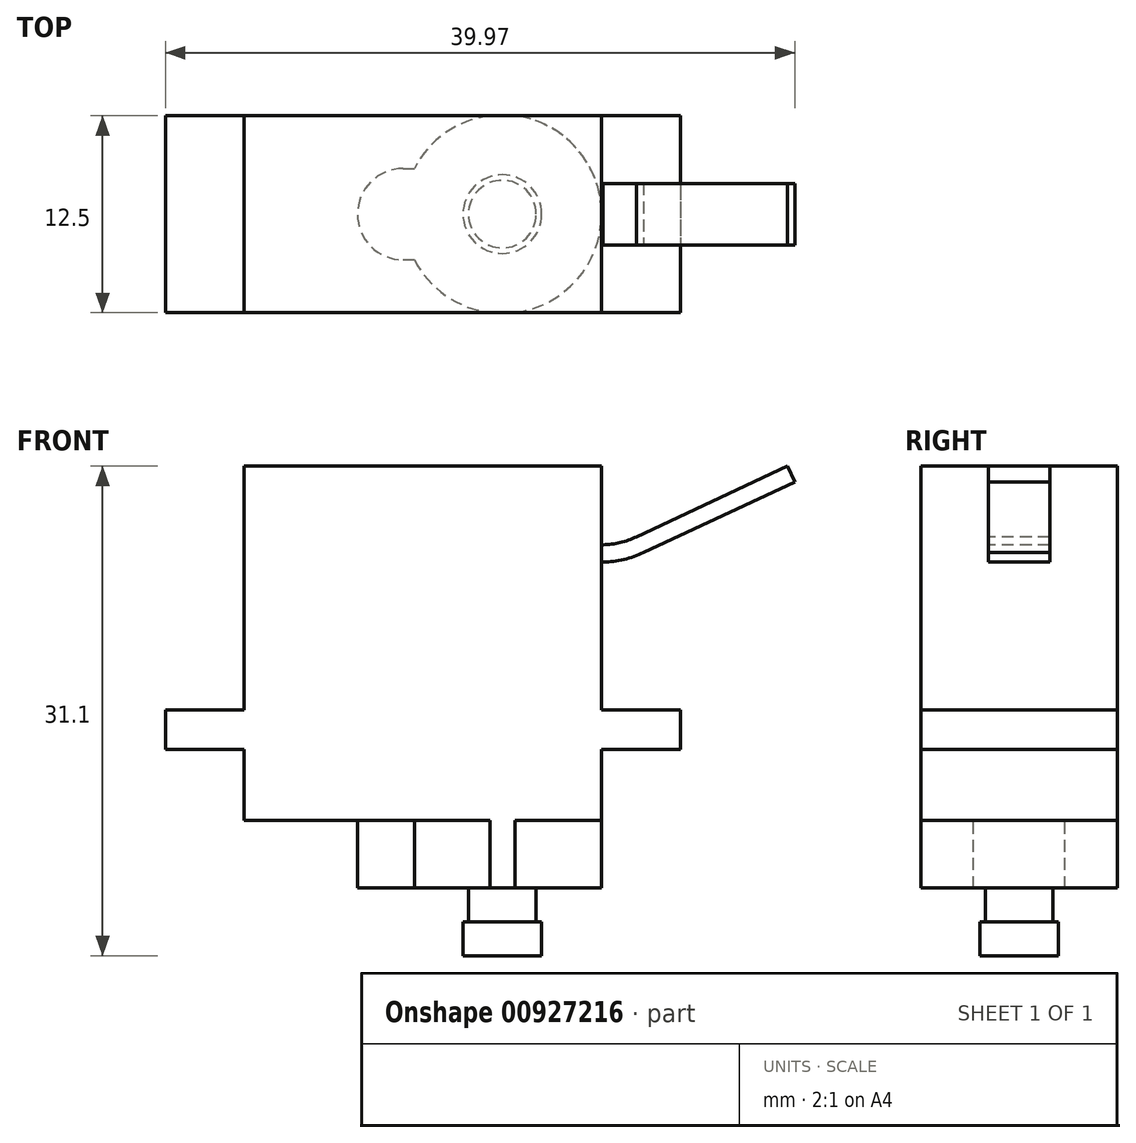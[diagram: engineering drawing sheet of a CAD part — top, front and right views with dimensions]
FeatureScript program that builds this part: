
annotation { "Feature Type Name" : "Feature", "Feature Type Description" : "" }
export const myFeature = defineFeature(function(context is Context, id is Id, definition is map)
    precondition{}
    {
        {
            var Q0;
            Q0=qCreatedBy(makeId("Top.planeOp"),FACE);
            var sketch = newSketch(context, id + "F0", { "sketchPlane" : qUnion([Q0])});
            skLineSegment(sketch, "E0.bottom", {"start": v(-4.5, 12.22) * mm, "end": v(18.2, 12.22) * mm});
            skLineSegment(sketch, "E0.top", {"start": v(-4.5, -0.28) * mm, "end": v(18.2, -0.28) * mm});
            skLineSegment(sketch, "E0.left", {"start": v(-4.5, 12.22) * mm, "end": v(-4.5, -0.28) * mm});
            skLineSegment(sketch, "E0.right", {"start": v(18.2, 12.22) * mm, "end": v(18.2, -0.28) * mm});
            skSolve(sketch);
        }
        {
            var Q0;
            Q0=qSketchRegion(id+"F0",true);
            extrude(context, id + "F1", {"entities" : qUnion([Q0]), "depth" : 22.5 * mm, "offsetDistance" : 25 * mm});
        }
        {
            var Q0;
            Q0=makeQuery(id+"F1.opExtrude","SWEPT_FACE",FACE,{"disambiguationData":[OSD([sQuery(id+"F0.wireOp",EDGE,"E0.left")])]});
            var sketch = newSketch(context, id + "F2", { "sketchPlane" : qUnion([Q0])});
            skLineSegment(sketch, "E1.bottom", {"start": v(0.28, 4.5) * mm, "end": v(-12.22, 4.5) * mm});
            skLineSegment(sketch, "E1.top", {"start": v(0.28, 7) * mm, "end": v(-12.22, 7) * mm});
            skLineSegment(sketch, "E1.left", {"start": v(0.28, 4.5) * mm, "end": v(0.28, 7) * mm});
            skLineSegment(sketch, "E1.right", {"start": v(-12.22, 4.5) * mm, "end": v(-12.22, 7) * mm});
            skSolve(sketch);
        }
        {
            var Q0;
            Q0=qSketchRegion(id+"F2",true);
            extrude(context, id + "F3", {"entities" : qUnion([Q0]), "operationType" : NewBodyOperationType.ADD, "depth" : 5 * mm, "offsetDistance" : 25 * mm});
        }
        {
            var Q0;
            Q0=makeQuery(id+"F1.opExtrude","SWEPT_FACE",FACE,{"disambiguationData":[OSD([sQuery(id+"F0.wireOp",EDGE,"E0.right")])]});
            var sketch = newSketch(context, id + "F4", { "sketchPlane" : qUnion([Q0])});
            skLineSegment(sketch, "E2.bottom", {"start": v(12.22, 4.5) * mm, "end": v(-0.28, 4.5) * mm});
            skLineSegment(sketch, "E2.top", {"start": v(12.22, 7) * mm, "end": v(-0.28, 7) * mm});
            skLineSegment(sketch, "E2.left", {"start": v(12.22, 4.5) * mm, "end": v(12.22, 7) * mm});
            skLineSegment(sketch, "E2.right", {"start": v(-0.28, 4.5) * mm, "end": v(-0.28, 7) * mm});
            skSolve(sketch);
        }
        {
            var Q0;
            Q0=qSketchRegion(id+"F4",true);
            extrude(context, id + "F5", {"entities" : qUnion([Q0]), "operationType" : NewBodyOperationType.ADD, "depth" : 5 * mm, "offsetDistance" : 25 * mm});
        }
        {
            var Q0;
            Q0=makeQuery(id+"F1.opExtrude","CAP_FACE",FACE,{"disambiguationData":[OSD([sQuery(id+"F0.wireOp",EDGE,"E0.bottom"),sQuery(id+"F0.wireOp",EDGE,"E0.top"),sQuery(id+"F0.wireOp",EDGE,"E0.left"),sQuery(id+"F0.wireOp",EDGE,"E0.right")])],"isStart":true});
            var sketch = newSketch(context, id + "F6", { "sketchPlane" : qUnion([Q0])});
            skArc(sketch, "E3", {"start": v(6.28, -8.8) * mm, "mid": v(18.2, -5.97) * mm, "end": v(6.28, -3.15) * mm});
            skLineSegment(sketch, "E4", {"start": v(11.9, 0.28) * mm, "end": v(11.9, -12.22) * mm, "construction": true});
            skArc(sketch, "E5", {"start": v(5.6, -3.07) * mm, "mid": v(2.7, -5.97) * mm, "end": v(5.6, -8.87) * mm});
            skLineSegment(sketch, "E6", {"start": v(18.2, -5.97) * mm, "end": v(-4.5, -5.97) * mm, "construction": true});
            skLineSegment(sketch, "E7", {"start": v(5.6, -3.07) * mm, "end": v(6.32, -3.07) * mm});
            skPoint(sketch, "E8", {"position": v(5.6, -3.07) * mm});
            skPoint(sketch, "E9", {"position": v(6.32, -3.07) * mm});
            skLineSegment(sketch, "E10", {"start": v(5.6, -8.87) * mm, "end": v(6.32, -8.87) * mm});
            skPoint(sketch, "E11", {"position": v(6.32, -8.87) * mm});
            skPoint(sketch, "E12", {"position": v(5.6, -8.87) * mm});
            skSolve(sketch);
        }
        {
            var Q0;
            Q0=makeQuery(id+"F6.imprint","IMPRINT",FACE,{"disambiguationData":[TD([[makeQuery(id+"F6.imprint","IMPRINT",EDGE,{"derivedFrom":sQuery(id+"F6.wireOp",EDGE,"E5")}),1.0]])]});
            extrude(context, id + "F7", {"entities" : qUnion([Q0]), "operationType" : NewBodyOperationType.ADD, "depth" : 4.3 * mm, "offsetDistance" : 25 * mm});
        }
        {
            var Q0;
            Q0=makeQuery(id+"F7.opExtrude","CAP_FACE",FACE,{"disambiguationData":[OSD([sQuery(id+"F0.wireOp",EDGE,"E0.bottom"),sQuery(id+"F0.wireOp",EDGE,"E0.top"),sQuery(id+"F6.wireOp",EDGE,"E3"),sQuery(id+"F6.wireOp",EDGE,"E5"),sQuery(id+"F6.wireOp",EDGE,"E7"),sQuery(id+"F6.wireOp",EDGE,"E10")])],"isStart":false});
            var sketch = newSketch(context, id + "F8", { "sketchPlane" : qUnion([Q0])});
            skCircle(sketch, "E13", {"center": v(11.9, -5.97) * mm, "radius": 2.15 * mm});
            skSolve(sketch);
        }
        {
            var Q0;
            Q0=qSketchRegion(id+"F8",true);
            extrude(context, id + "F9", {"entities" : qUnion([Q0]), "operationType" : NewBodyOperationType.ADD, "depth" : 2.15 * mm, "offsetDistance" : 25 * mm});
        }
        {
            var Q0;
            Q0=makeQuery(id+"F9.opExtrude","CAP_FACE",FACE,{"disambiguationData":[OSD([sQuery(id+"F8.wireOp",EDGE,"E13")])],"isStart":false});
            var sketch = newSketch(context, id + "F10", { "sketchPlane" : qUnion([Q0])});
            skCircle(sketch, "E14", {"center": v(11.9, -5.97) * mm, "radius": 2.5 * mm});
            skSolve(sketch);
        }
        {
            var Q0;
            Q0=qSketchRegion(id+"F10",true);
            extrude(context, id + "F11", {"entities" : qUnion([Q0]), "operationType" : NewBodyOperationType.ADD, "depth" : 2.15 * mm, "offsetDistance" : 25 * mm});
        }
        {
            var Q0;
            {var subQ1=sQuery(id+"F0.wireOp",EDGE,"E0.right");Q0=makeQuery(id+"F5.boolean.opBoolean","SPLIT",FACE,{"disambiguationData":[TD([makeQuery(id+"F5.opExtrude","SWEPT_FACE",FACE,{"disambiguationData":[OSD([sQuery(id+"F4.wireOp",EDGE,"E2.top")])]})])],"derivedFrom":makeQuery(id+"F1.opExtrude","SWEPT_FACE",FACE,{"disambiguationData":[OSD([subQ1])]})});}
            var sketch = newSketch(context, id + "F12", { "sketchPlane" : qUnion([Q0])});
            skLineSegment(sketch, "E15.bottom", {"start": v(7.92, 17.5) * mm, "end": v(4.02, 17.5) * mm});
            skLineSegment(sketch, "E15.top", {"start": v(7.92, 16.4) * mm, "end": v(4.02, 16.4) * mm});
            skLineSegment(sketch, "E15.left", {"start": v(7.92, 17.5) * mm, "end": v(7.92, 16.4) * mm});
            skLineSegment(sketch, "E15.right", {"start": v(4.02, 17.5) * mm, "end": v(4.02, 16.4) * mm});
            skLineSegment(sketch, "E16", {"start": v(5.97, 22.5) * mm, "end": v(5.97, 7) * mm, "construction": true});
            skPoint(sketch, "E17", {"position": v(5.97, 17.5) * mm});
            skSolve(sketch);
        }
        {
            var Q0;
            Q0=qSketchRegion(id+"F12",true);
            extrude(context, id + "F13", {"entities" : qUnion([Q0]), "operationType" : NewBodyOperationType.ADD, "depth" : .1 * mm, "offsetDistance" : 25 * mm});
        }
        {
            var Q0;
            Q0=makeQuery(id+"F13.opExtrude","CAP_FACE",FACE,{"disambiguationData":[OSD([sQuery(id+"F12.wireOp",EDGE,"E15.bottom"),sQuery(id+"F12.wireOp",EDGE,"E15.top"),sQuery(id+"F12.wireOp",EDGE,"E15.left"),sQuery(id+"F12.wireOp",EDGE,"E15.right")])],"isStart":false});
            var Q1;
            Q1=makeQuery(id+"F1.opExtrude","CAP_EDGE",EDGE,{"disambiguationData":[OSD([sQuery(id+"F0.wireOp",EDGE,"E0.right")])],"isStart":false});
            revolve(context, id + "F14", {"operationType" : NewBodyOperationType.ADD, "surfaceOperationType" : NewSurfaceOperationType.NEW, "entities" : qUnion([Q0]), "axis" : qUnion([Q1]), "revolveType" : RevolveType.ONE_DIRECTION, "angle" : 25 * degree});
        }
        {
            var Q0;
            Q0=makeQuery(id+"F14.opRevolve","CAP_FACE",FACE,{"disambiguationData":[OSD([sQuery(id+"F12.wireOp",EDGE,"E15.bottom"),sQuery(id+"F12.wireOp",EDGE,"E15.top"),sQuery(id+"F12.wireOp",EDGE,"E15.left"),sQuery(id+"F12.wireOp",EDGE,"E15.right")])],"isStart":false});
            var sketch = newSketch(context, id + "F15", { "sketchPlane" : qUnion([Q0])});
            skLineSegment(sketch, "E18.0", {"start": v(7.92, 6.6) * mm, "end": v(4.02, 6.6) * mm});
            skLineSegment(sketch, "E18.1", {"start": v(7.92, 7.7) * mm, "end": v(7.92, 6.6) * mm});
            skLineSegment(sketch, "E18.2", {"start": v(7.92, 7.7) * mm, "end": v(4.02, 7.7) * mm});
            skLineSegment(sketch, "E18.3", {"start": v(4.02, 7.7) * mm, "end": v(4.02, 6.6) * mm});
            skSolve(sketch);
        }
        {
            var Q0;
            Q0=qSketchRegion(id+"F15",true);
            extrude(context, id + "F16", {"entities" : qUnion([Q0]), "operationType" : NewBodyOperationType.ADD, "depth" : 10.6 * mm, "offsetDistance" : 25 * mm});
        }
    });
